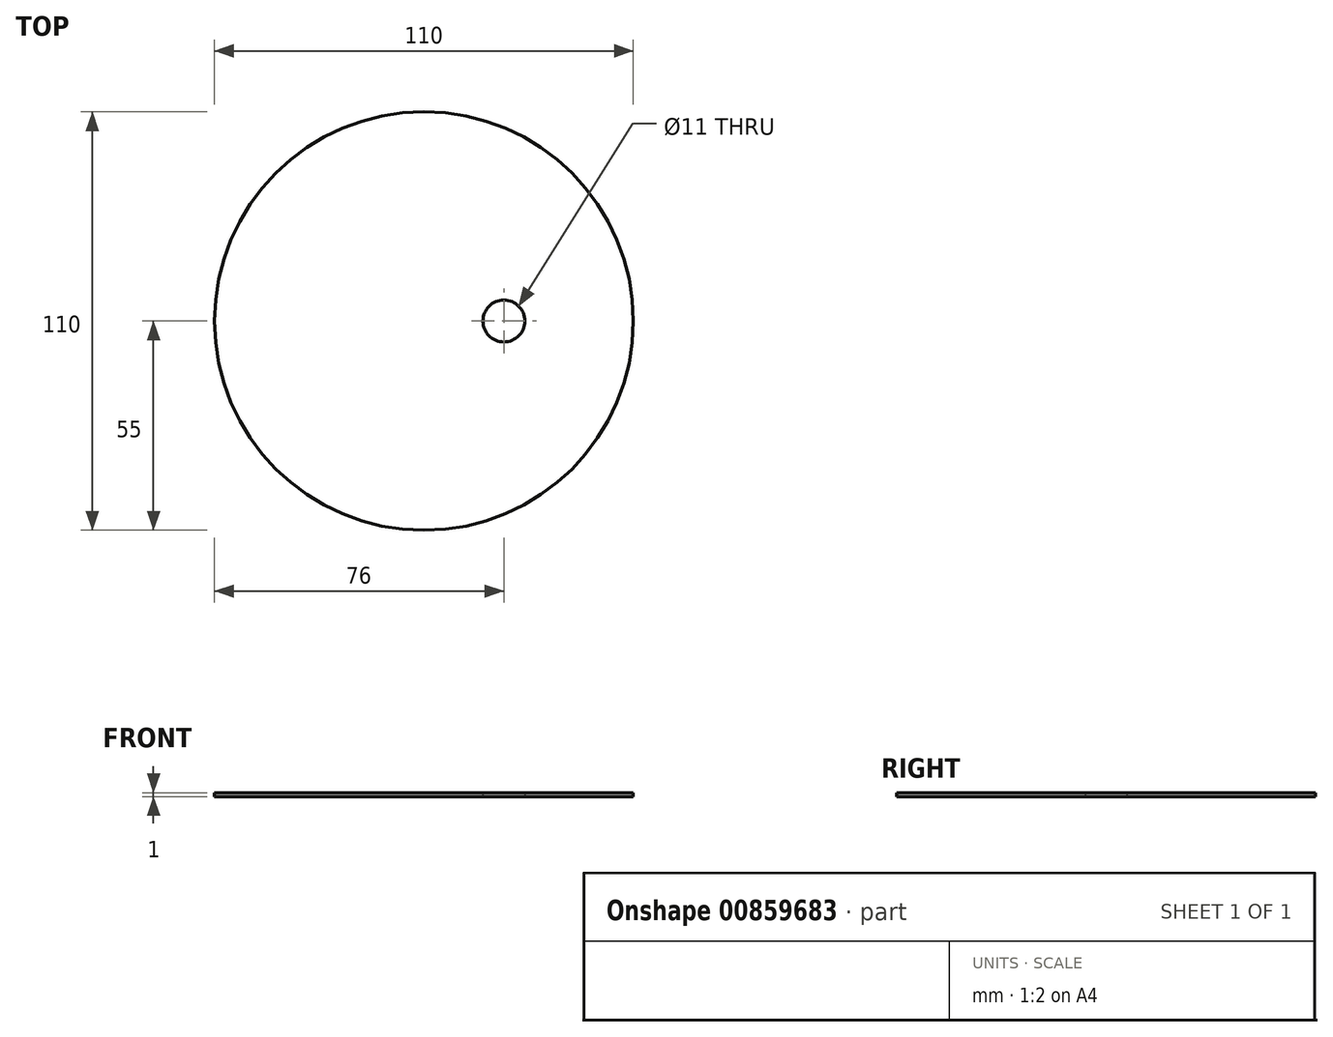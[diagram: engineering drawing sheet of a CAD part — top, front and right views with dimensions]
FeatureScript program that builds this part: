
annotation { "Feature Type Name" : "Feature", "Feature Type Description" : "" }
export const myFeature = defineFeature(function(context is Context, id is Id, definition is map)
    precondition{}
    {
        {
            var Q0;
            Q0=qCreatedBy(makeId("Top.planeOp"),FACE);
            var sketch = newSketch(context, id + "F0", { "sketchPlane" : qUnion([Q0])});
            skCircle(sketch, "E0.0.0", {"center": v(0, 0) * mm, "radius": 55 * mm});
            skCircle(sketch, "E1.0", {"center": v(21, 0) * mm, "radius": 5.5 * mm});
            skSolve(sketch);
        }
        {
            var Q0;
            Q0=makeQuery(id+"F0.imprint","IMPRINT",FACE,{"disambiguationData":[TD([[makeQuery(id+"F0.imprint","IMPRINT",EDGE,{"derivedFrom":sQuery(id+"F0.wireOp",EDGE,"E0.0.0")}),1.0]])]});
            extrude(context, id + "F1", {"entities" : qUnion([Q0]), "depth" : 1 * mm, "offsetDistance" : 25 * mm});
        }
    });
